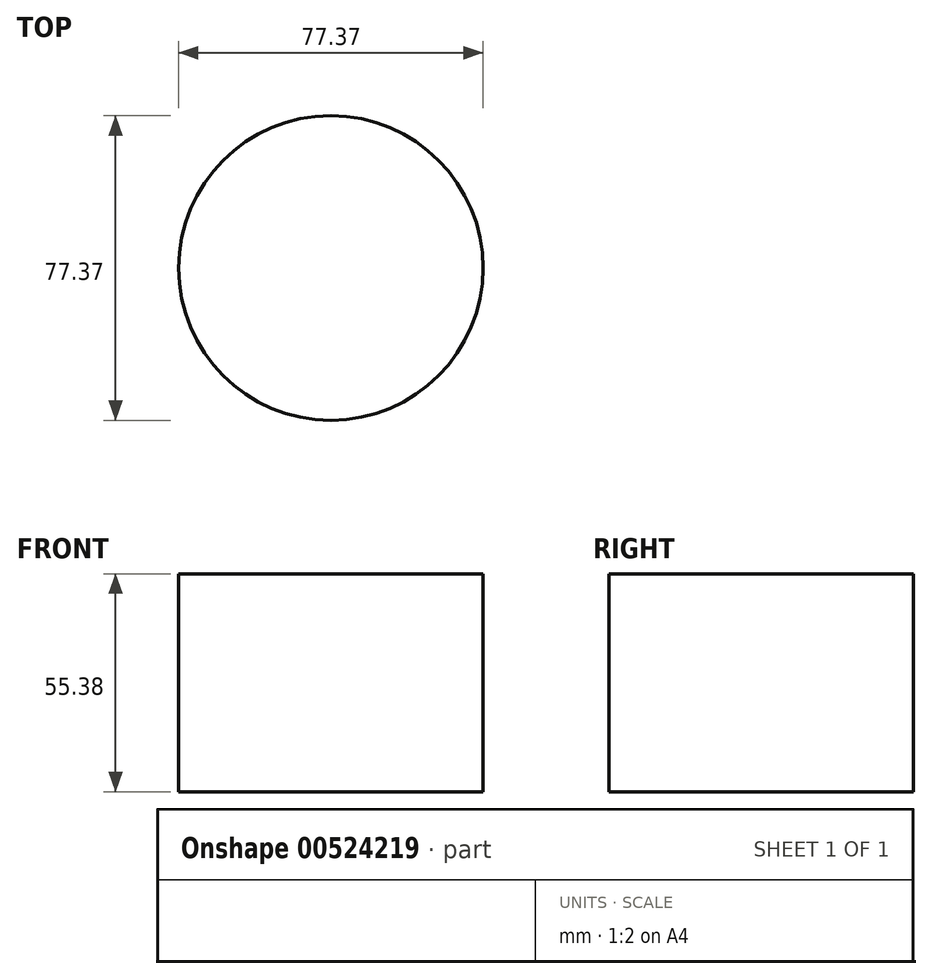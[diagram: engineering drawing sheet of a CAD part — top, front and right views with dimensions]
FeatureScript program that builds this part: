
annotation { "Feature Type Name" : "Feature", "Feature Type Description" : "" }
export const myFeature = defineFeature(function(context is Context, id is Id, definition is map)
    precondition{}
    {
        {
            var Q0;
            Q0=qCreatedBy(makeId("Top.planeOp"),FACE);
            cPlane(context, id + "F0", {"entities" : qUnion([Q0]), "cplaneType" : CPlaneType.OFFSET, "offset" : 90.42 * mm, "width" : 152.4 * mm, "height" : 152.4 * mm});
        }
        {
            var Q0;
            Q0=qCreatedBy(id+"F0.planeOp",FACE);
            var sketch = newSketch(context, id + "F1", { "sketchPlane" : qUnion([Q0])});
            skCircle(sketch, "E0", {"center": v(35.82, -30.04) * mm, "radius": 38.69 * mm});
            skSolve(sketch);
        }
        {
            var Q0;
            Q0=makeQuery(id+"F1.imprint","IMPRINT",FACE,{"disambiguationData":[TD([[makeQuery(id+"F1.imprint","IMPRINT",EDGE,{"derivedFrom":sQuery(id+"F1.wireOp",EDGE,"E0")}),1.0]])]});
            extrude(context, id + "F2", {"entities" : qUnion([Q0]), "depth" : 55.37 * mm, "offsetDistance" : 25.4 * mm});
        }
    });
